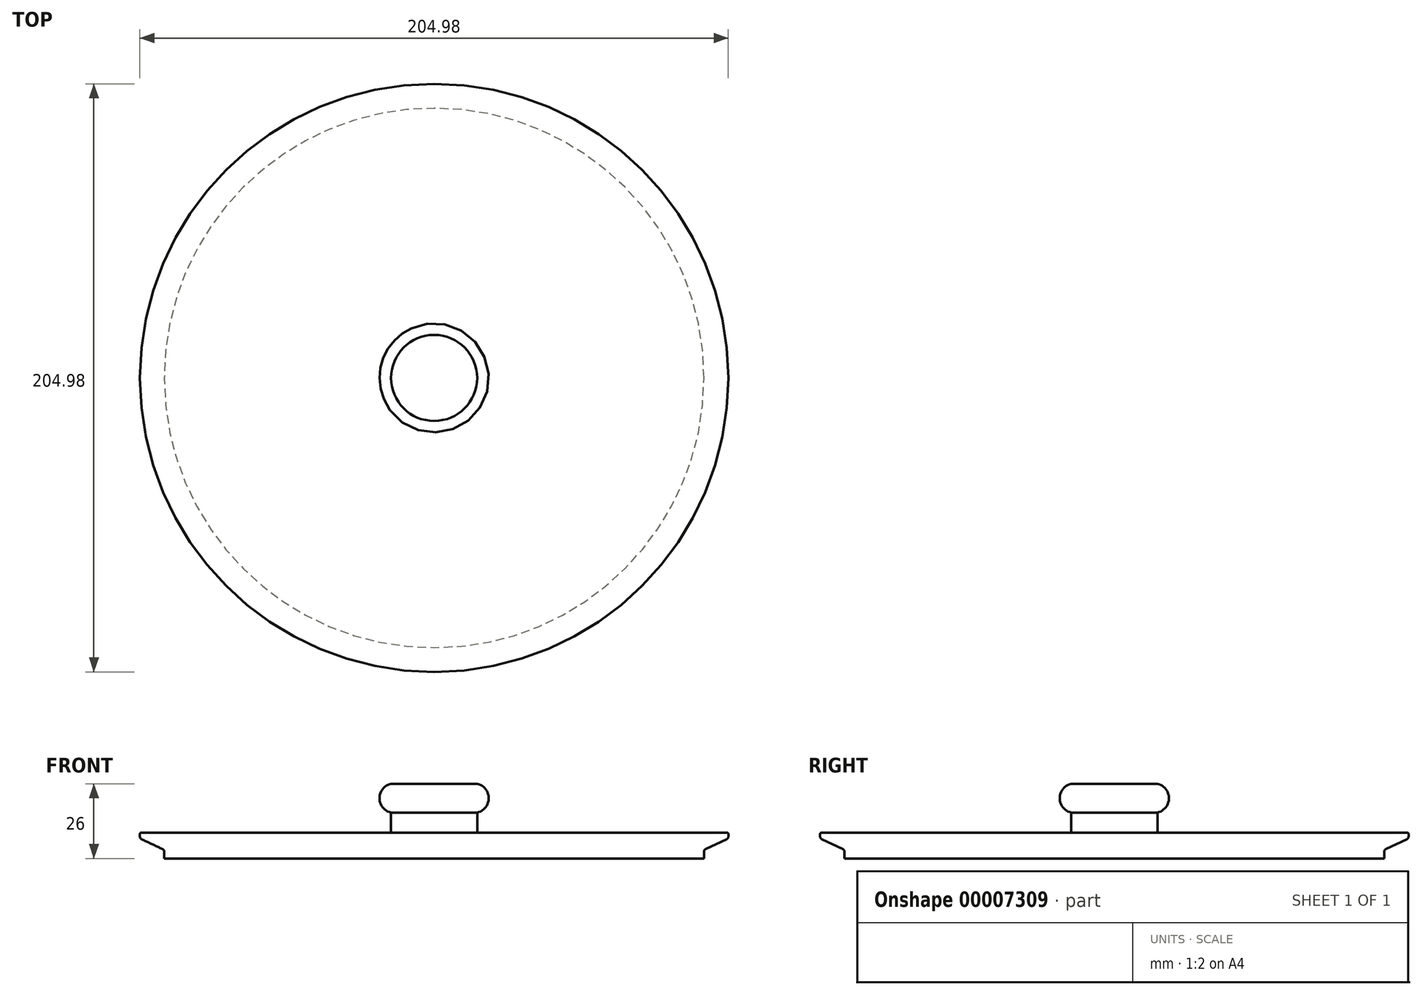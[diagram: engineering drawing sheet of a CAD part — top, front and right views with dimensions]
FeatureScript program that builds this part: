
annotation { "Feature Type Name" : "Feature", "Feature Type Description" : "" }
export const myFeature = defineFeature(function(context is Context, id is Id, definition is map)
    precondition{}
    {
        {
            var Q0;
            Q0=qCreatedBy(makeId("Front.planeOp"),FACE);
            var sketch = newSketch(context, id + "F0", { "sketchPlane" : qUnion([Q0])});
            skLineSegment(sketch, "E0.bottom", {"start": v(0, 0) * mm, "end": v(94, 0) * mm});
            skLineSegment(sketch, "E0.top", {"start": v(0, 2.97) * mm, "end": v(94, 2.97) * mm});
            skLineSegment(sketch, "E0.left", {"start": v(0, 0) * mm, "end": v(0, 2.97) * mm});
            skLineSegment(sketch, "E0.right", {"start": v(94, 0) * mm, "end": v(94, 4.77) * mm});
            skLineSegment(sketch, "E1.left", {"start": v(94, 0) * mm, "end": v(94, 2.33) * mm});
            skLineSegment(sketch, "E2.right", {"start": v(0, 2) * mm, "end": v(0, 6) * mm});
            skPoint(sketch, "E3.visualSharp", {"position": v(94, 2.97) * mm});
            skLineSegment(sketch, "E4.bottom", {"start": v(0, 6) * mm, "end": v(15, 6) * mm});
            skLineSegment(sketch, "E5.top", {"start": v(0, 26) * mm, "end": v(15, 26) * mm});
            skLineSegment(sketch, "E5.left", {"start": v(0, 6) * mm, "end": v(0, 26) * mm});
            skLineSegment(sketch, "E5.right", {"start": v(15, 6) * mm, "end": v(15, 26) * mm});
            skPoint(sketch, "E6", {"position": v(15, 16) * mm});
            skArc(sketch, "E7", {"start": v(15, 16) * mm, "mid": v(19.02, 21) * mm, "end": v(15, 26) * mm});
            skLineSegment(sketch, "E8.bottom", {"start": v(0, 2.97) * mm, "end": v(91.03, 2.97) * mm});
            skLineSegment(sketch, "E8.top", {"start": v(0, 6.97) * mm, "end": v(102.5, 6.97) * mm});
            skLineSegment(sketch, "E8.left", {"start": v(0, 2.97) * mm, "end": v(0, 6.97) * mm});
            skPoint(sketch, "E9.visualSharp", {"position": v(102.5, 6.97) * mm});
            skArc(sketch, "E9.filletArc", {"start": v(102.5, 6.97) * mm, "mid": v(102.5, 5.4) * mm, "end": v(102.5, 6.97) * mm});
            skLineSegment(sketch, "E10.left", {"start": v(94, 0) * mm, "end": v(94, 0.2) * mm});
            skLineSegment(sketch, "E11.left", {"start": v(94, 0.2) * mm, "end": v(94, 0.4) * mm});
            skLineSegment(sketch, "E12.right", {"start": v(94, 0.4) * mm, "end": v(94, 0.6) * mm});
            skLineSegment(sketch, "E13.right", {"start": v(94, 0.6) * mm, "end": v(94, 0.8) * mm});
            skLineSegment(sketch, "E14.right", {"start": v(94, 0.8) * mm, "end": v(94, 1) * mm});
            skLineSegment(sketch, "E15.right", {"start": v(94, 1) * mm, "end": v(94, 1.2) * mm});
            skLineSegment(sketch, "E16.right", {"start": v(94, 1.2) * mm, "end": v(94, 1.4) * mm});
            skLineSegment(sketch, "E17.bottom", {"start": v(102.5, 6.97) * mm, "end": v(0, 6.97) * mm});
            skLineSegment(sketch, "E17.top", {"start": v(102.04, 8.97) * mm, "end": v(0, 8.97) * mm});
            skLineSegment(sketch, "E17.left", {"start": v(102.5, 7.6) * mm, "end": v(102.5, 8.52) * mm});
            skLineSegment(sketch, "E17.right", {"start": v(0, 6.97) * mm, "end": v(0, 8.97) * mm});
            skPoint(sketch, "E18.visualSharp", {"position": v(102.5, 8.97) * mm});
            skArc(sketch, "E18.filletArc", {"start": v(102.5, 8.52) * mm, "mid": v(102.36, 8.84) * mm, "end": v(102.04, 8.97) * mm});
            skLineSegment(sketch, "E19", {"start": v(101.92, 6.7) * mm, "end": v(94.57, 3.24) * mm});
            skArc(sketch, "E20.filletArc", {"start": v(94.57, 3.24) * mm, "mid": v(94.16, 2.87) * mm, "end": v(94, 2.33) * mm});
            skArc(sketch, "E21.filletArc", {"start": v(101.92, 6.7) * mm, "mid": v(102.34, 7.07) * mm, "end": v(102.5, 7.6) * mm});
            skSolve(sketch);
        }
        {
            var Q0;
            Q0 = qSketchRegion(id + "F0", true);
            var Q1;
            Q1=sQuery(id+"F0.wireOp",EDGE,"E2.right");
            revolve(context, id + "F1", {"entities" : qUnion([Q0]), "axis" : qUnion([Q1]), "revolveType" : RevolveType.FULL});
        }
    });
